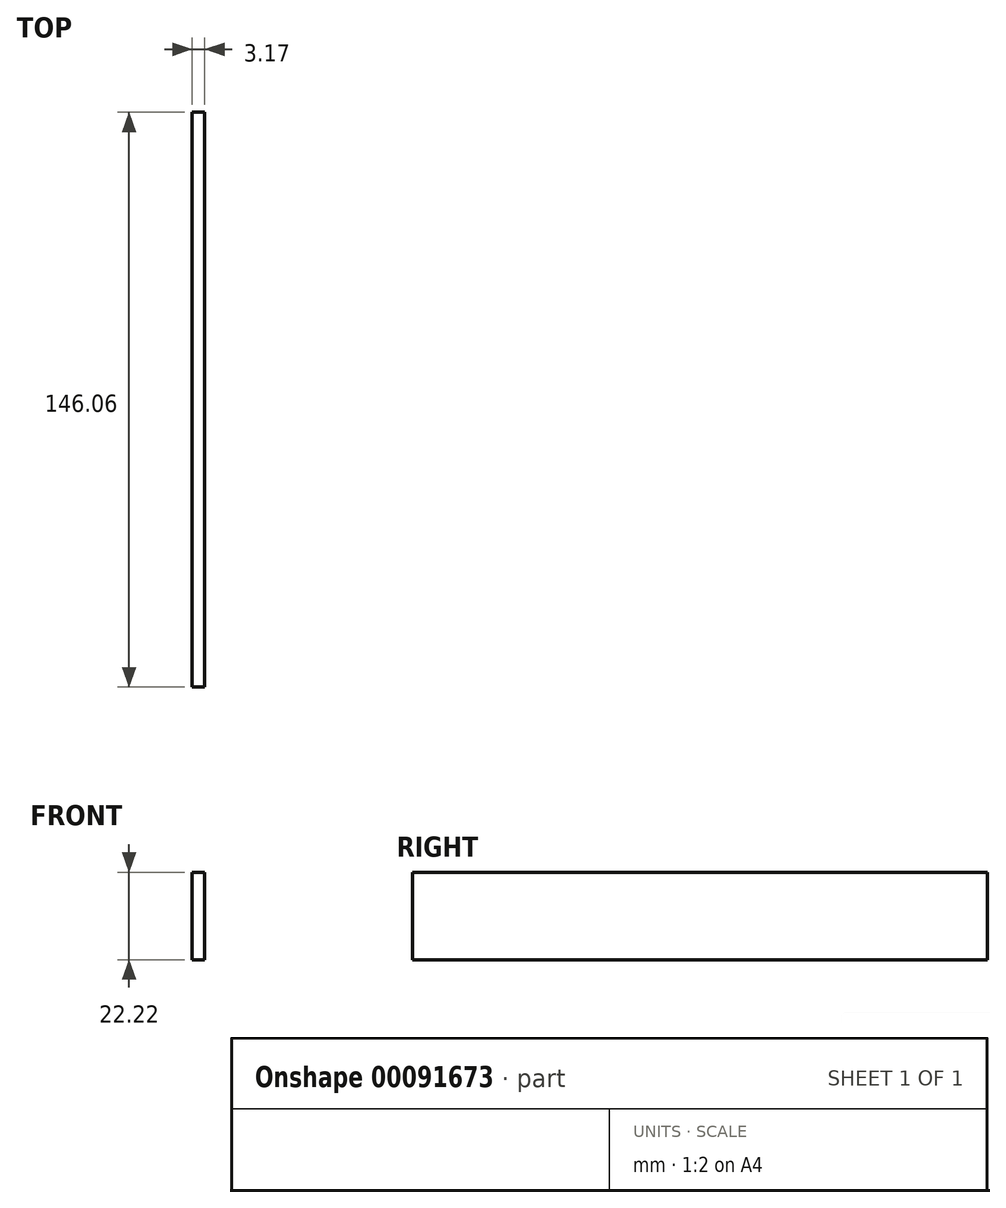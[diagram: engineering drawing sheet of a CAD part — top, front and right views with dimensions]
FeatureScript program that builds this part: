
annotation { "Feature Type Name" : "Feature", "Feature Type Description" : "" }
export const myFeature = defineFeature(function(context is Context, id is Id, definition is map)
    precondition{}
    {
        {
            var Q0;
            Q0=qCreatedBy(makeId("Right.planeOp"),FACE);
            var sketch = newSketch(context, id + "F0", { "sketchPlane" : qUnion([Q0])});
            skLineSegment(sketch, "E0.bottom", {"start": v(-73.03, 11.11) * mm, "end": v(73.03, 11.11) * mm});
            skLineSegment(sketch, "E0.top", {"start": v(-73.03, -11.11) * mm, "end": v(73.03, -11.11) * mm});
            skLineSegment(sketch, "E0.left", {"start": v(-73.03, 11.11) * mm, "end": v(-73.03, -11.11) * mm});
            skLineSegment(sketch, "E0.right", {"start": v(73.03, 11.11) * mm, "end": v(73.03, -11.11) * mm});
            skPoint(sketch, "E0.middle", {"position": v(0, 0) * mm});
            skSolve(sketch);
        }
        {
            var Q0;
            Q0=makeQuery(id+"F0.imprint","IMPRINT",FACE,{"disambiguationData":[TD([[makeQuery(id+"F0.imprint","IMPRINT",EDGE,{"derivedFrom":sQuery(id+"F0.wireOp",EDGE,"E0.bottom")}),-1.0]])]});
            extrude(context, id + "F1", {"entities" : qUnion([Q0]), "depth" : 3.17 * mm});
        }
        {
            var Q0;
            Q0=makeQuery(id+"F1.opExtrude","CAP_FACE",FACE,{"disambiguationData":[OSD([sQuery(id+"F0.wireOp",EDGE,"E0.bottom"),sQuery(id+"F0.wireOp",EDGE,"E0.top"),sQuery(id+"F0.wireOp",EDGE,"E0.left"),sQuery(id+"F0.wireOp",EDGE,"E0.right")])],"isStart":false});
            var sketch = newSketch(context, id + "F2", { "sketchPlane" : qUnion([Q0])});
            skPoint(sketch, "E1", {"position": v(-40.64, 0) * mm});
            skPoint(sketch, "E2", {"position": v(0, 0) * mm});
            skPoint(sketch, "E3", {"position": v(40.64, 0) * mm});
            skSolve(sketch);
        }
    });
